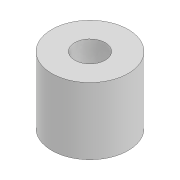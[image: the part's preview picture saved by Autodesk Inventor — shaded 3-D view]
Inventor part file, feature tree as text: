
AUTODESK INVENTOR PART (.ipt)
format: ipt  version: 2022 (Build 260153000, 153)  size: 80,896 bytes
history: native  units: mm
features: extrude x1, sketch x1
ambient origin geometry x8: Origin, YZ Plane, XZ Plane, XY Plane, X Axis, Y Axis, Z Axis, Center Point
bodies: Solid1 (feature_tree)
feature tree (2):
  extrude  "Extrusion1"  Depth=7.0mm
  sketch  "Sketch1"  dims[d0=3.2mm d1=8.0mm d2=7.0mm d3=0.0mm]
